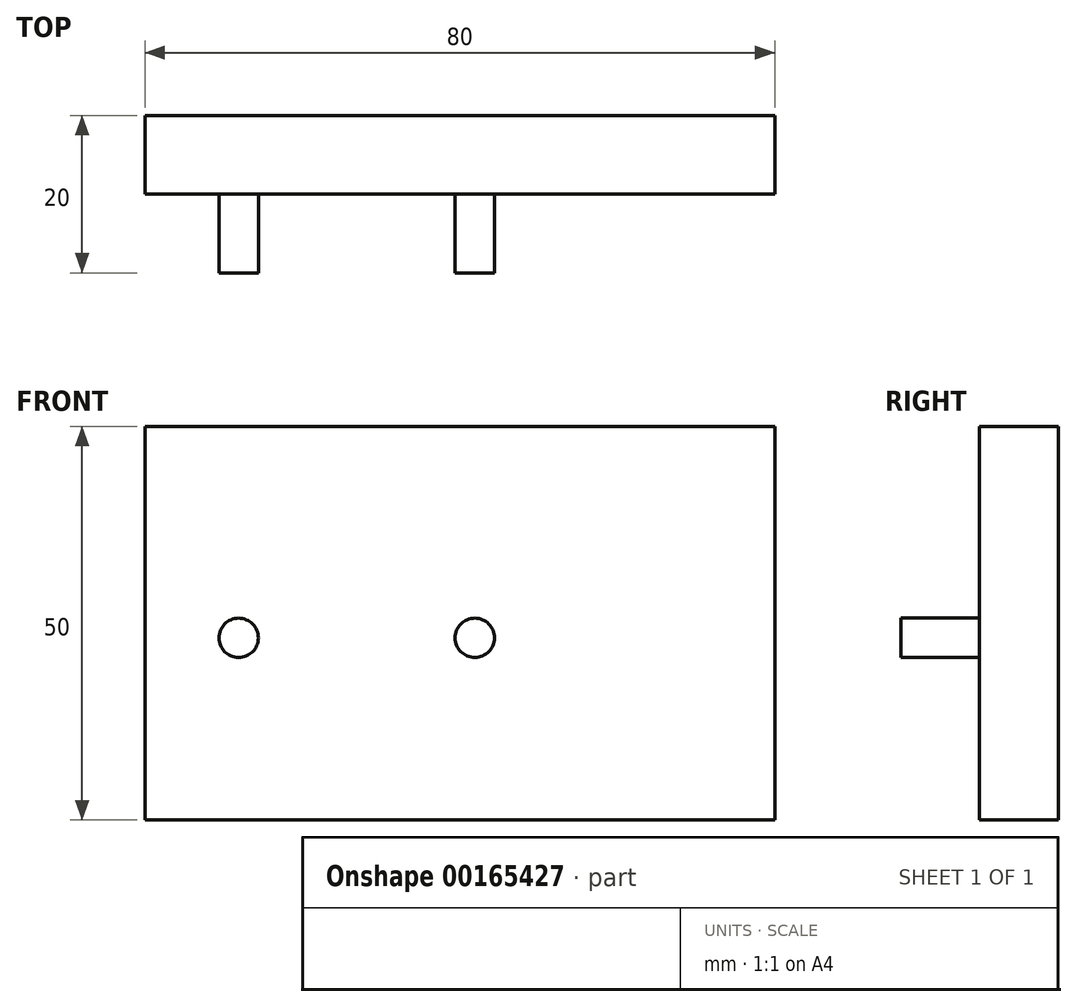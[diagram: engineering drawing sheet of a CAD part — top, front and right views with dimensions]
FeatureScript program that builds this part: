
annotation { "Feature Type Name" : "Feature", "Feature Type Description" : "" }
export const myFeature = defineFeature(function(context is Context, id is Id, definition is map)
    precondition{}
    {
        {
            var Q0;
            Q0=qCreatedBy(makeId("Front.planeOp"),FACE);
            var sketch = newSketch(context, id + "F0", { "sketchPlane" : qUnion([Q0])});
            skLineSegment(sketch, "E0.bottom", {"start": v(-21.9, 26.86) * mm, "end": v(58.1, 26.86) * mm});
            skLineSegment(sketch, "E0.top", {"start": v(-21.9, -23.14) * mm, "end": v(58.1, -23.14) * mm});
            skLineSegment(sketch, "E0.left", {"start": v(-21.9, 26.86) * mm, "end": v(-21.9, -23.14) * mm});
            skLineSegment(sketch, "E0.right", {"start": v(58.1, 26.86) * mm, "end": v(58.1, -23.14) * mm});
            skSolve(sketch);
        }
        {
            var Q0;
            Q0=makeQuery(id+"F0.imprint","IMPRINT",FACE,{"disambiguationData":[TD([[makeQuery(id+"F0.imprint","IMPRINT",EDGE,{"derivedFrom":sQuery(id+"F0.wireOp",EDGE,"E0.bottom")}),-1.0]])]});
            extrude(context, id + "F1", {"entities" : qUnion([Q0]), "depth" : 10 * mm});
        }
        {
            var Q0;
            Q0=makeQuery(id+"F1.opExtrude","CAP_FACE",FACE,{"disambiguationData":[OSD([sQuery(id+"F0.wireOp",EDGE,"E0.bottom"),sQuery(id+"F0.wireOp",EDGE,"E0.top"),sQuery(id+"F0.wireOp",EDGE,"E0.left"),sQuery(id+"F0.wireOp",EDGE,"E0.right")])],"isStart":false});
            var sketch = newSketch(context, id + "F2", { "sketchPlane" : qUnion([Q0])});
            skLineSegment(sketch, "E1", {"start": v(0, 0) * mm, "end": v(-10, 0) * mm});
            skCircle(sketch, "E2", {"center": v(-10, 0) * mm, "radius": 2.5 * mm});
            skSolve(sketch);
        }
        {
            var Q0;
            Q0=makeQuery(id+"F2.imprint","IMPRINT",FACE,{"disambiguationData":[TD([[makeQuery(id+"F2.imprint","IMPRINT",EDGE,{"derivedFrom":sQuery(id+"F2.wireOp",EDGE,"E2")}),1.0]])]});
            extrude(context, id + "F3", {"entities" : qUnion([Q0]), "operationType" : NewBodyOperationType.ADD, "depth" : 10 * mm});
        }
        {
            var Q0;
            Q0=makeQuery(id+"F1.opExtrude","CAP_FACE",FACE,{"disambiguationData":[OSD([sQuery(id+"F0.wireOp",EDGE,"E0.bottom"),sQuery(id+"F0.wireOp",EDGE,"E0.top"),sQuery(id+"F0.wireOp",EDGE,"E0.left"),sQuery(id+"F0.wireOp",EDGE,"E0.right")])],"isStart":false});
            var sketch = newSketch(context, id + "F4", { "sketchPlane" : qUnion([Q0])});
            skLineSegment(sketch, "E3", {"start": v(0, 0) * mm, "end": v(20, 0) * mm});
            skCircle(sketch, "E4", {"center": v(20, 0) * mm, "radius": 2.5 * mm});
            skSolve(sketch);
        }
        {
            var Q0;
            Q0=makeQuery(id+"F4.imprint","IMPRINT",FACE,{"disambiguationData":[TD([[makeQuery(id+"F4.imprint","IMPRINT",EDGE,{"derivedFrom":sQuery(id+"F4.wireOp",EDGE,"E4")}),1.0]])]});
            extrude(context, id + "F5", {"entities" : qUnion([Q0]), "operationType" : NewBodyOperationType.ADD, "depth" : 10 * mm});
        }
    });
